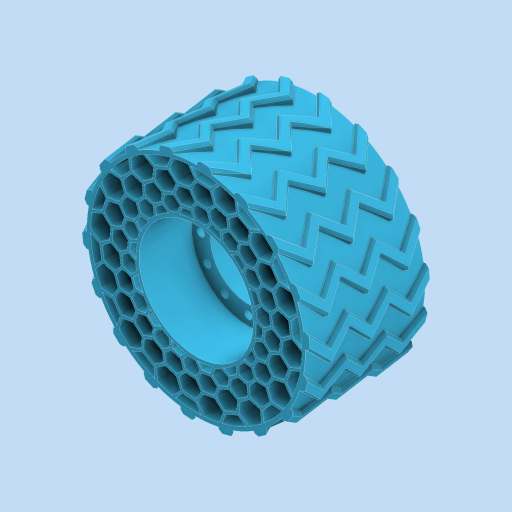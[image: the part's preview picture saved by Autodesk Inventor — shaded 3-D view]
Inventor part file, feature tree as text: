
AUTODESK INVENTOR PART (.ipt)
format: ipt  version: 2023 (Build 270158000, 158)  size: 1,232,896 bytes
history: native  units: in
note: dims shown in document units (in); Inventor stores cm internally (conversion verified against a paired STEP export)
features: extrude x21, other x18, thicken_offset x17, sketch x5, pattern_circular x2, plane x2, mirror x1, sweep x1
ambient origin geometry x8: Origin, YZ Plane, XZ Plane, XY Plane, X Axis, Y Axis, Z Axis, Center Point
bodies: Solid1 (feature_tree)
feature tree (67):
  sketch  "Sketch1"  dims[d0=3.1496in d1=0.0in d2=3.1496in d3=0.0in]
  extrude  "Extrusion1"  Depth=3.1496in TaperAngle=0.0deg
  thicken_offset  "Thicken1"
  thicken_offset  "Thicken2"
  thicken_offset  "Thicken3"
  thicken_offset  "Thicken4"
  thicken_offset  "Thicken5"
  thicken_offset  "Thicken6"
  thicken_offset  "Thicken7"
  thicken_offset  "Thicken8"
  thicken_offset  "Thicken9"
  thicken_offset  "Thicken10"
  thicken_offset  "Thicken11"
  thicken_offset  "Thicken12"
  thicken_offset  "Thicken13"
  thicken_offset  "Thicken14"
  thicken_offset  "Thicken15"
  thicken_offset  "Thicken16"
  thicken_offset  "Thicken17"
  pattern_circular  "Circular Pattern1"  Count=8  [1 undecoded]
  sketch  "Sketch2"  dims[d4=0.0945in d5=3.1496in d6=0.0in]
  extrude  "Extrusion2"  Depth=3.1496in TaperAngle=0.0deg
  plane  "Work Plane1"
  mirror  "Mirror1"
  extrude  "Extrusion3"  Depth=3.1496in TaperAngle=0.0deg
  sketch  "Sketch3"  dims[d7=0.063in d8=3.1496in d9=0.0in]
  other  "Work Point1"
  plane  "Work Plane2"
  sweep  "Sweep1"
  extrude  "Extrusion4"  Depth=0.063in
  pattern_circular  "Circular Pattern2"  Count=8  [1 undecoded]
  other  "Srf1"
  other  "Srf2"
  other  "Srf3"
  other  "Srf4"
  other  "Srf5"
  other  "Srf6"
  other  "Srf7"
  other  "Srf8"
  other  "Srf9"
  other  "Srf10"
  other  "Srf11"
  other  "Srf12"
  other  "Srf13"
  other  "Srf14"
  other  "Srf15"
  other  "Srf16"
  other  "Srf17"
  sketch  "Sketch4"  dims[d10=0.063in d11=3.1496in d12=0.0in]
  sketch  "Sketch5"  dims[d13=0.063in d14=3.1496in d15=0.0in d16=0.063in d17=3.1496in d18=0.0in d19=0.063in d20=3.1496in d21=0.0in d22=0.063in d23=3.1496in d24=0.0in d25=0.063in d26=3.1496in d27=0.0in d28=0.063in d29=3.1496in d30=0.0in d31=0.063in d32=3.1496in d33=0.0in d34=0.063in d35=3.1496in d36=0.0in d37=0.063in d38=3.1496in d39=0.0in d40=0.063in d41=3.1496in d42=0.0in d43=0.063in d44=3.1496in d45=0.0in d46=0.063in d47=3.1496in d48=0.0in d49=0.063in d50=3.1496in d51=0.0in d52=0.063in d53=5.5118in d54=360.0deg d57=2.5in d58=0.19in d59=4.7244in d61=360.0deg d63=1.378in d64=0.0in d65=0.5in d66=0.0in d67=0.0in d68=0.002in d69=0.3937in d70=0.126in d71=0.0787in d72=0.0787in d73=0.0787in d74=0.0787in d75=0.0in d76=0.0in d77=0.0in d78=0.0in d79=7.0866in d80=360.0deg d82=3.0in d83=0.5in]
  extrude  "ExtrusionSrf1"  Depth=0.063in
  extrude  "ExtrusionSrf2"  Depth=3.1496in TaperAngle=0.0deg
  extrude  "ExtrusionSrf3"  Depth=0.063in
  extrude  "ExtrusionSrf4"  Depth=3.1496in TaperAngle=0.0deg
  extrude  "ExtrusionSrf5"  Depth=0.063in
  extrude  "ExtrusionSrf6"  Depth=3.1496in TaperAngle=0.0deg
  extrude  "ExtrusionSrf7"  Depth=0.063in
  extrude  "ExtrusionSrf8"  Depth=3.1496in TaperAngle=0.0deg
  extrude  "ExtrusionSrf9"  Depth=0.063in
  extrude  "ExtrusionSrf10"  Depth=3.1496in TaperAngle=0.0deg
  extrude  "ExtrusionSrf11"  Depth=0.063in
  extrude  "ExtrusionSrf12"  Depth=3.1496in TaperAngle=0.0deg
  extrude  "ExtrusionSrf13"  Depth=0.063in
  extrude  "ExtrusionSrf14"  Depth=3.1496in TaperAngle=0.0deg
  extrude  "ExtrusionSrf15"  Depth=0.063in
  extrude  "ExtrusionSrf16"  Depth=3.1496in TaperAngle=0.0deg
  extrude  "ExtrusionSrf17"  Depth=0.063in
note: 2 required parameter values undecoded (feature->parameter linkage not recoverable at this tier; creation-order binding heuristic only, values carry confidence <= 0.55)
